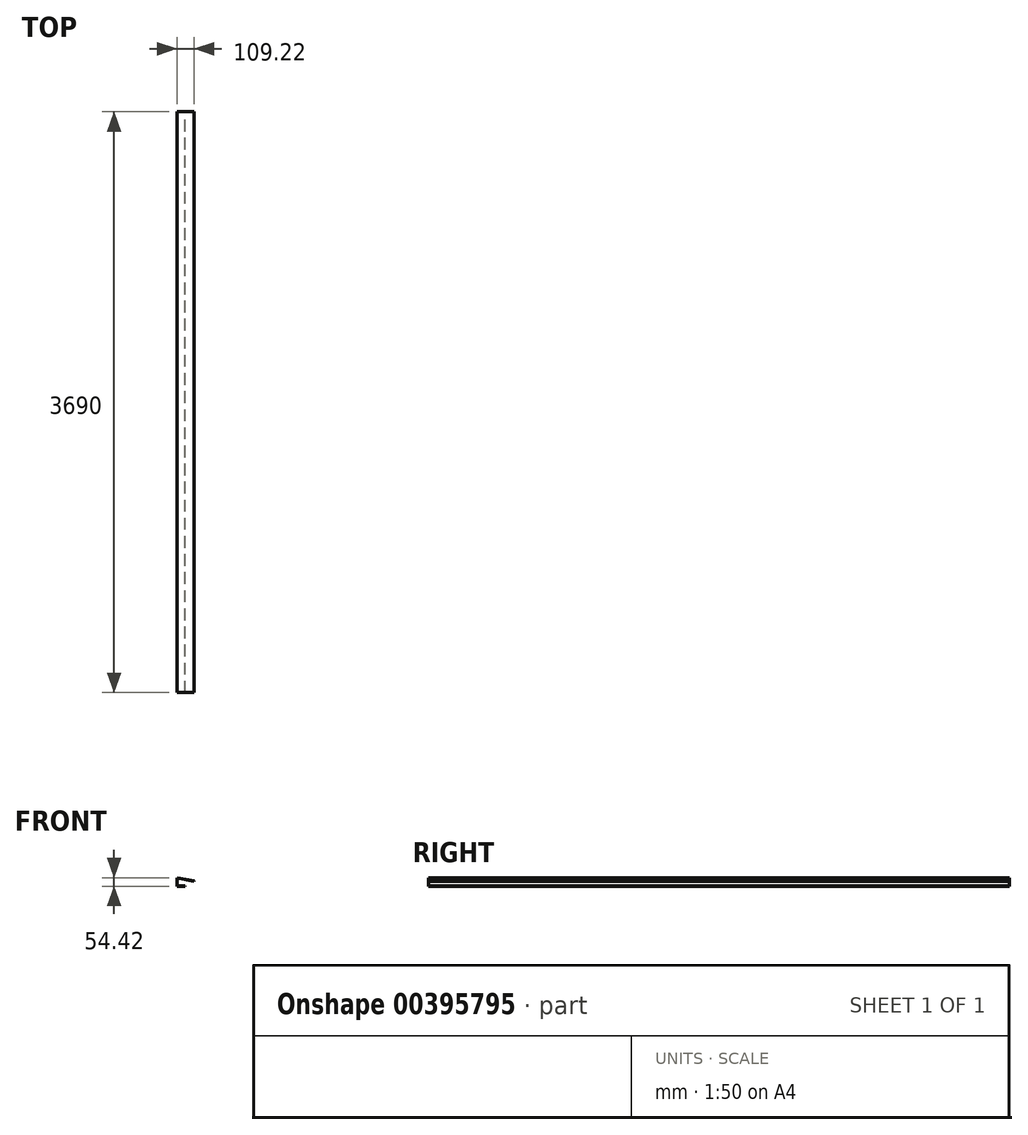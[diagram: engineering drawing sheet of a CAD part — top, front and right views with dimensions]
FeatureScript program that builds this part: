
annotation { "Feature Type Name" : "Feature", "Feature Type Description" : "" }
export const myFeature = defineFeature(function(context is Context, id is Id, definition is map)
    precondition{}
    {
        {
            var Q0;
            Q0=qCreatedBy(makeId("Front.planeOp"),FACE);
            var sketch = newSketch(context, id + "F0", { "sketchPlane" : qUnion([Q0])});
            skLineSegment(sketch, "E0", {"start": v(0, 0) * mm, "end": v(50, 0) * mm});
            skLineSegment(sketch, "E1", {"start": v(50, 0) * mm, "end": v(50, 2) * mm});
            skLineSegment(sketch, "E2", {"start": v(50, 2) * mm, "end": v(42, 2) * mm});
            skLineSegment(sketch, "E3", {"start": v(42, 2) * mm, "end": v(2, 2) * mm});
            skLineSegment(sketch, "E4", {"start": v(2, 2) * mm, "end": v(2, 52) * mm});
            skLineSegment(sketch, "E5", {"start": v(2, 52) * mm, "end": v(108.84, 31.57) * mm});
            skLineSegment(sketch, "E6", {"start": v(108.84, 31.57) * mm, "end": v(109.22, 33.53) * mm});
            skLineSegment(sketch, "E7", {"start": v(109.22, 33.53) * mm, "end": v(0, 54.42) * mm});
            skLineSegment(sketch, "E8", {"start": v(0, 54.42) * mm, "end": v(0, 0) * mm});
            skSolve(sketch);
        }
        {
            var Q0;
            Q0=qSketchRegion(id+"F0",true);
            extrude(context, id + "F1", {"entities" : qUnion([Q0]), "depth" : 3690 * mm, "offsetDistance" : 25 * mm});
        }
    });
